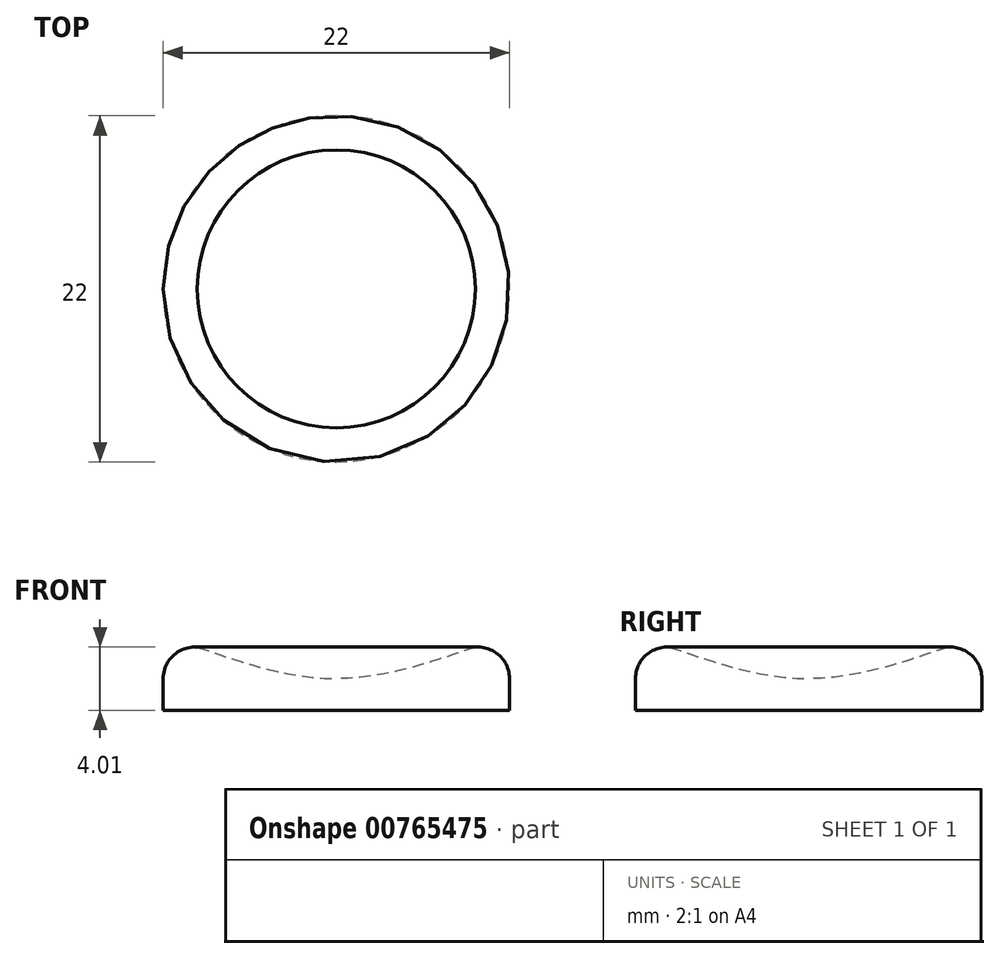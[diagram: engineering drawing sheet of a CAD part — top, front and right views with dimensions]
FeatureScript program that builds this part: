
annotation { "Feature Type Name" : "Feature", "Feature Type Description" : "" }
export const myFeature = defineFeature(function(context is Context, id is Id, definition is map)
    precondition{}
    {
        {
            var Q0;
            Q0=qCreatedBy(makeId("Right.planeOp"),FACE);
            var sketch = newSketch(context, id + "F0", { "sketchPlane" : qUnion([Q0])});
            skLineSegment(sketch, "E0.left", {"start": v(11, 1) * mm, "end": v(11, -1) * mm});
            skPoint(sketch, "E0.middle", {"position": v(0, 0) * mm});
            skLineSegment(sketch, "E1.MirrorCS", {"start": v(8.83, 3) * mm, "end": v(8.83, 3) * mm});
            skLineSegment(sketch, "E2.MirrorCS", {"start": v(11, 1) * mm, "end": v(11, 1) * mm});
            skPoint(sketch, "E3.visualSharp", {"position": v(11, 3.19) * mm});
            skArc(sketch, "E3.filletArc", {"start": v(11, 1) * mm, "mid": v(10.36, 2.48) * mm, "end": v(8.83, 3) * mm});
            skLineSegment(sketch, "E4", {"start": v(0, -1) * mm, "end": v(0, 1) * mm});
            skLineSegment(sketch, "E5", {"start": v(11, -1) * mm, "end": v(0, -1) * mm});
            skFitSpline(sketch, "E6", {"points": [v(8.83, 3) * mm, v(0, 1) * mm], "startDerivative": vector(-9.17, -3.07) * mm, "endDerivative": vector(-9.53, -0.08) * mm});
            skSolve(sketch);
        }
        {
            var Q0;
            Q0 = qSketchRegion(id + "F0", true);
            var Q1;
            Q1=sQuery(id+"F0.wireOp",EDGE,"E4");
            revolve(context, id + "F1", {"surfaceOperationType" : NewSurfaceOperationType.NEW, "entities" : qUnion([Q0]), "axis" : qUnion([Q1]), "revolveType" : RevolveType.FULL});
        }
    });
